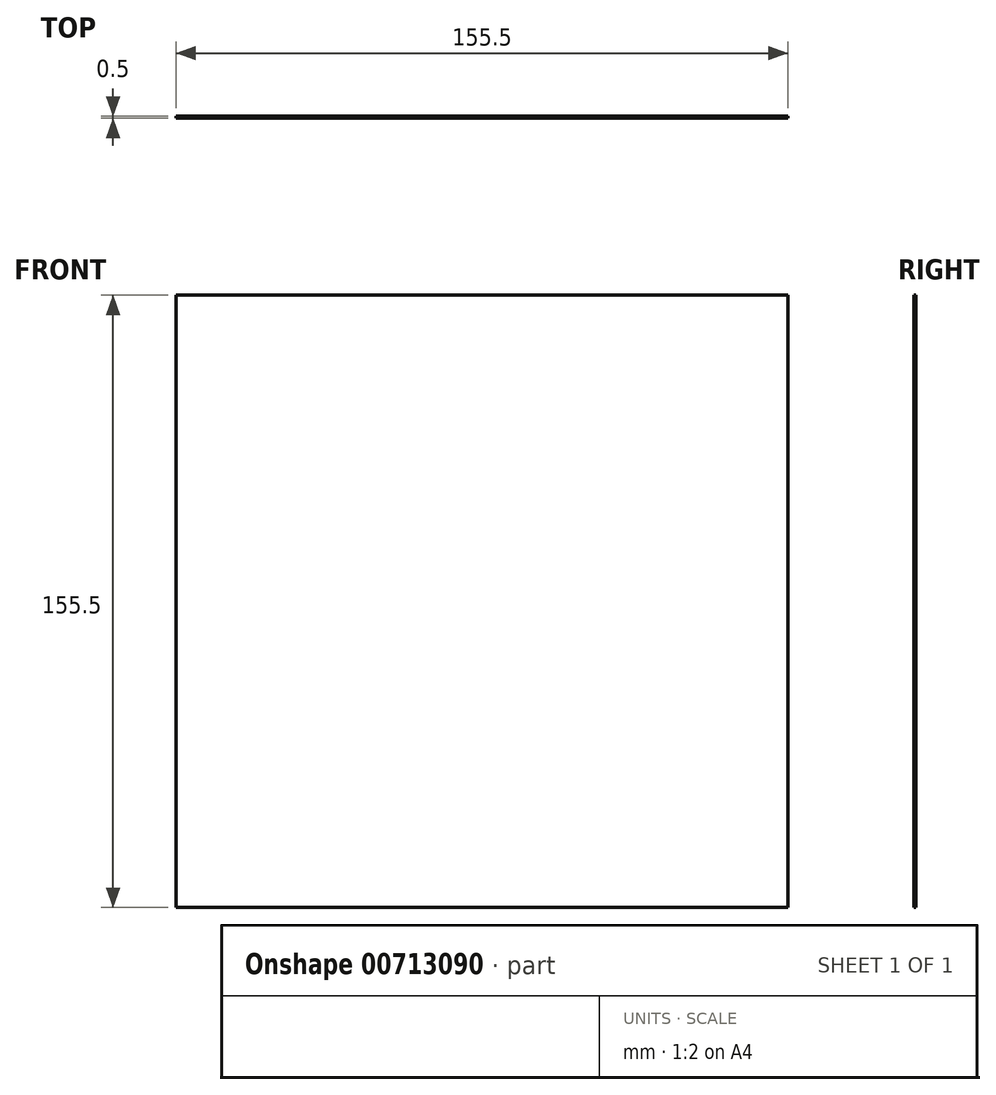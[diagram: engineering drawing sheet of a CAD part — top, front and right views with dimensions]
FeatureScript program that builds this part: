
annotation { "Feature Type Name" : "Feature", "Feature Type Description" : "" }
export const myFeature = defineFeature(function(context is Context, id is Id, definition is map)
    precondition{}
    {
        {
            var Q0;
            Q0=qCreatedBy(makeId("Front.planeOp"),FACE);
            var sketch = newSketch(context, id + "F0", { "sketchPlane" : qUnion([Q0])});
            skLineSegment(sketch, "E0.bottom", {"start": v(0, 0) * mm, "end": v(155.5, 0) * mm});
            skLineSegment(sketch, "E0.top", {"start": v(0, 155.5) * mm, "end": v(155.5, 155.5) * mm});
            skLineSegment(sketch, "E0.left", {"start": v(0, 0) * mm, "end": v(0, 155.5) * mm});
            skLineSegment(sketch, "E0.right", {"start": v(155.5, 0) * mm, "end": v(155.5, 155.5) * mm});
            skSolve(sketch);
        }
        {
            var Q0;
            Q0 = qSketchRegion(id + "F0", true);
            extrude(context, id + "F1", {"entities" : qUnion([Q0]), "depth" : 0.5 * mm, "offsetDistance" : 25 * mm});
        }
    });
